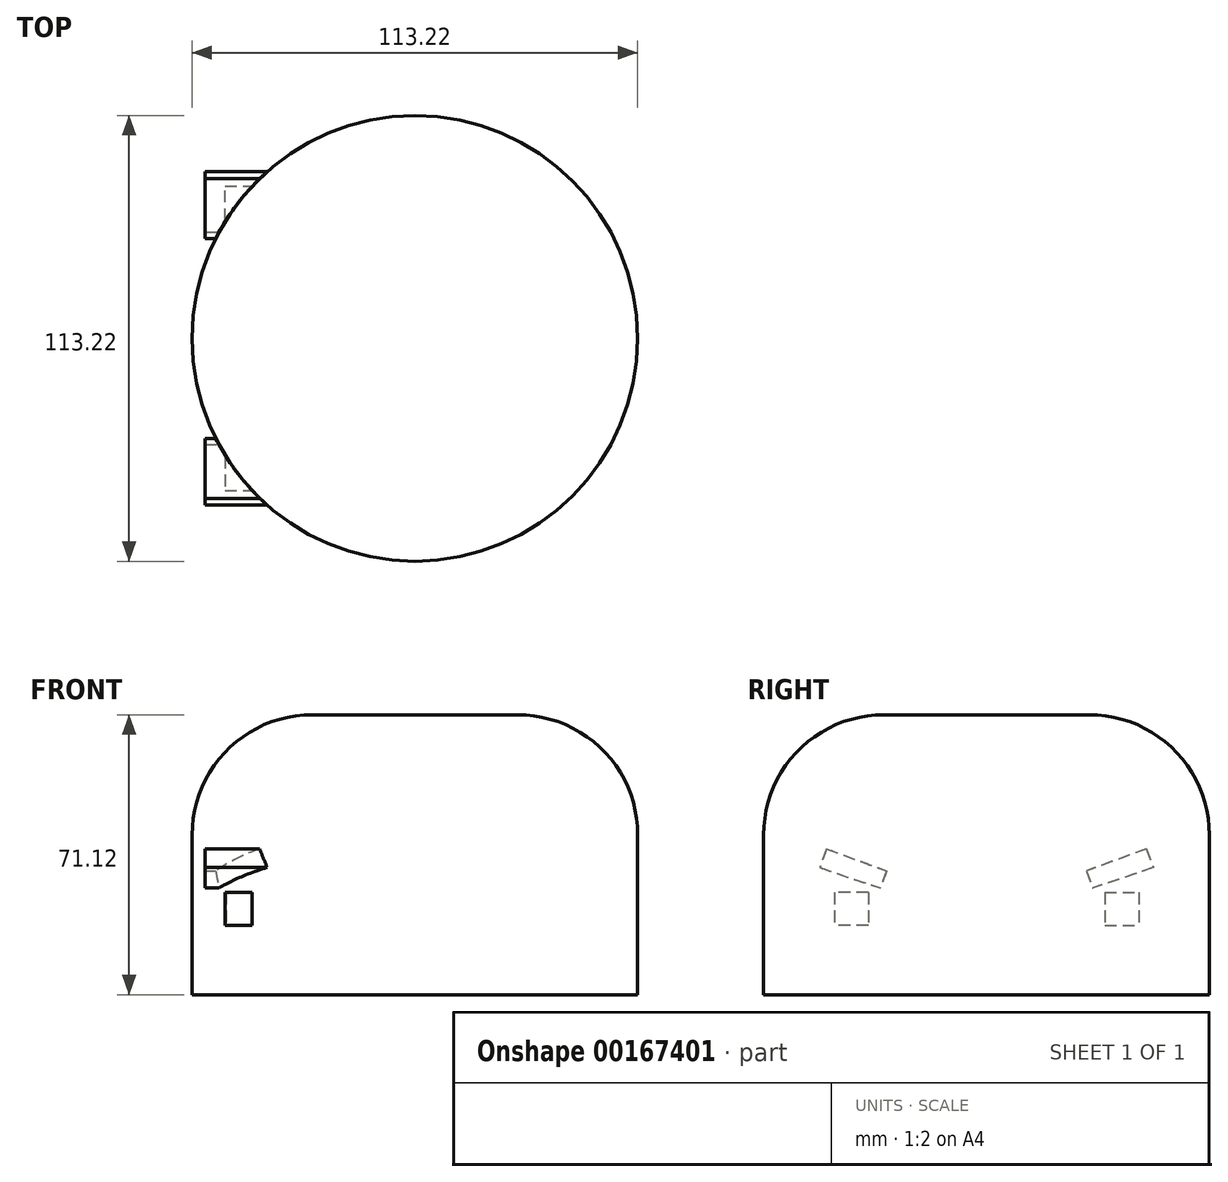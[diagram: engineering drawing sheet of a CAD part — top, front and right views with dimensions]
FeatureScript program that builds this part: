
annotation { "Feature Type Name" : "Feature", "Feature Type Description" : "" }
export const myFeature = defineFeature(function(context is Context, id is Id, definition is map)
    precondition{}
    {
        {
            var Q0;
            Q0=qCreatedBy(makeId("Top.planeOp"),FACE);
            var sketch = newSketch(context, id + "F0", { "sketchPlane" : qUnion([Q0])});
            skCircle(sketch, "E0", {"center": v(0, 0) * mm, "radius": 56.6 * mm});
            skSolve(sketch);
        }
        {
            var Q0;
            Q0=makeQuery(id+"F0.imprint","IMPRINT",FACE,{"disambiguationData":[TD([[makeQuery(id+"F0.imprint","IMPRINT",EDGE,{"derivedFrom":sQuery(id+"F0.wireOp",EDGE,"E0")}),1.0]])]});
            extrude(context, id + "F1", {"entities" : qUnion([Q0]), "depth" : 71.12 * mm});
        }
        {
            var Q0;
            Q0=makeQuery(id+"F1.opExtrude","CAP_EDGE",EDGE,{"disambiguationData":[OSD([sQuery(id+"F0.wireOp",EDGE,"E0")])],"isStart":false});
            fillet(context, id + "F2", {"entities" : qUnion([Q0]), "radius" : 30.48 * mm, "tangentPropagation" : true, "allowEdgeOverflow" : false});
        }
        {
            var Q0;
            Q0=qCreatedBy(makeId("Right.planeOp"),FACE);
            var sketch = newSketch(context, id + "F3", { "sketchPlane" : qUnion([Q0])});
            skLineSegment(sketch, "E1.bottom", {"start": v(30.03, 17.62) * mm, "end": v(38.66, 17.62) * mm});
            skLineSegment(sketch, "E1.top", {"start": v(30.03, 25.99) * mm, "end": v(38.66, 25.99) * mm});
            skLineSegment(sketch, "E1.left", {"start": v(30.03, 17.62) * mm, "end": v(30.03, 25.99) * mm});
            skLineSegment(sketch, "E1.right", {"start": v(38.66, 17.62) * mm, "end": v(38.66, 25.99) * mm});
            skPoint(sketch, "E1.middle", {"position": v(34.34, 21.8) * mm});
            skPoint(sketch, "E2.MirrorP", {"position": v(-34.34, 21.8) * mm});
            skLineSegment(sketch, "E3.MirrorCS", {"start": v(-30.03, 17.62) * mm, "end": v(-30.03, 25.99) * mm});
            skLineSegment(sketch, "E4.MirrorCS", {"start": v(-30.03, 25.99) * mm, "end": v(-38.66, 25.99) * mm});
            skLineSegment(sketch, "E5.MirrorCS", {"start": v(-38.66, 17.62) * mm, "end": v(-38.66, 25.99) * mm});
            skLineSegment(sketch, "E6.MirrorCS", {"start": v(-30.03, 17.62) * mm, "end": v(-38.66, 17.62) * mm});
            skSolve(sketch);
        }
        {
            var Q0;
            Q0 = qSketchRegion(id + "F3", true);
            extrude(context, id + "F4", {"entities" : qUnion([Q0]), "operationType" : NewBodyOperationType.ADD, "oppositeDirection" : true, "depth" : 48.26 * mm});
        }
        {
            var Q0;
            Q0=qCreatedBy(makeId("Right.planeOp"),FACE);
            var sketch = newSketch(context, id + "F5", { "sketchPlane" : qUnion([Q0])});
            skLineSegment(sketch, "E7", {"start": v(40.63, 37.05) * mm, "end": v(25.37, 31.44) * mm});
            skLineSegment(sketch, "E8", {"start": v(25.37, 31.44) * mm, "end": v(26.98, 27.07) * mm});
            skLineSegment(sketch, "E9", {"start": v(40.63, 37.05) * mm, "end": v(42.37, 32.3) * mm});
            skLineSegment(sketch, "E10", {"start": v(42.37, 32.3) * mm, "end": v(26.98, 27.07) * mm});
            skLineSegment(sketch, "E11.MirrorCS", {"start": v(-25.37, 31.44) * mm, "end": v(-26.98, 27.07) * mm});
            skLineSegment(sketch, "E12.MirrorCS", {"start": v(-40.63, 37.05) * mm, "end": v(-25.37, 31.44) * mm});
            skLineSegment(sketch, "E13.MirrorCS", {"start": v(-42.37, 32.3) * mm, "end": v(-26.98, 27.07) * mm});
            skLineSegment(sketch, "E14.MirrorCS", {"start": v(-40.63, 37.05) * mm, "end": v(-42.37, 32.3) * mm});
            skSolve(sketch);
        }
        {
            var Q0;
            Q0 = qSketchRegion(id + "F5", true);
            extrude(context, id + "F6", {"entities" : qUnion([Q0]), "operationType" : NewBodyOperationType.ADD, "oppositeDirection" : true, "depth" : 53.34 * mm});
        }
    });
